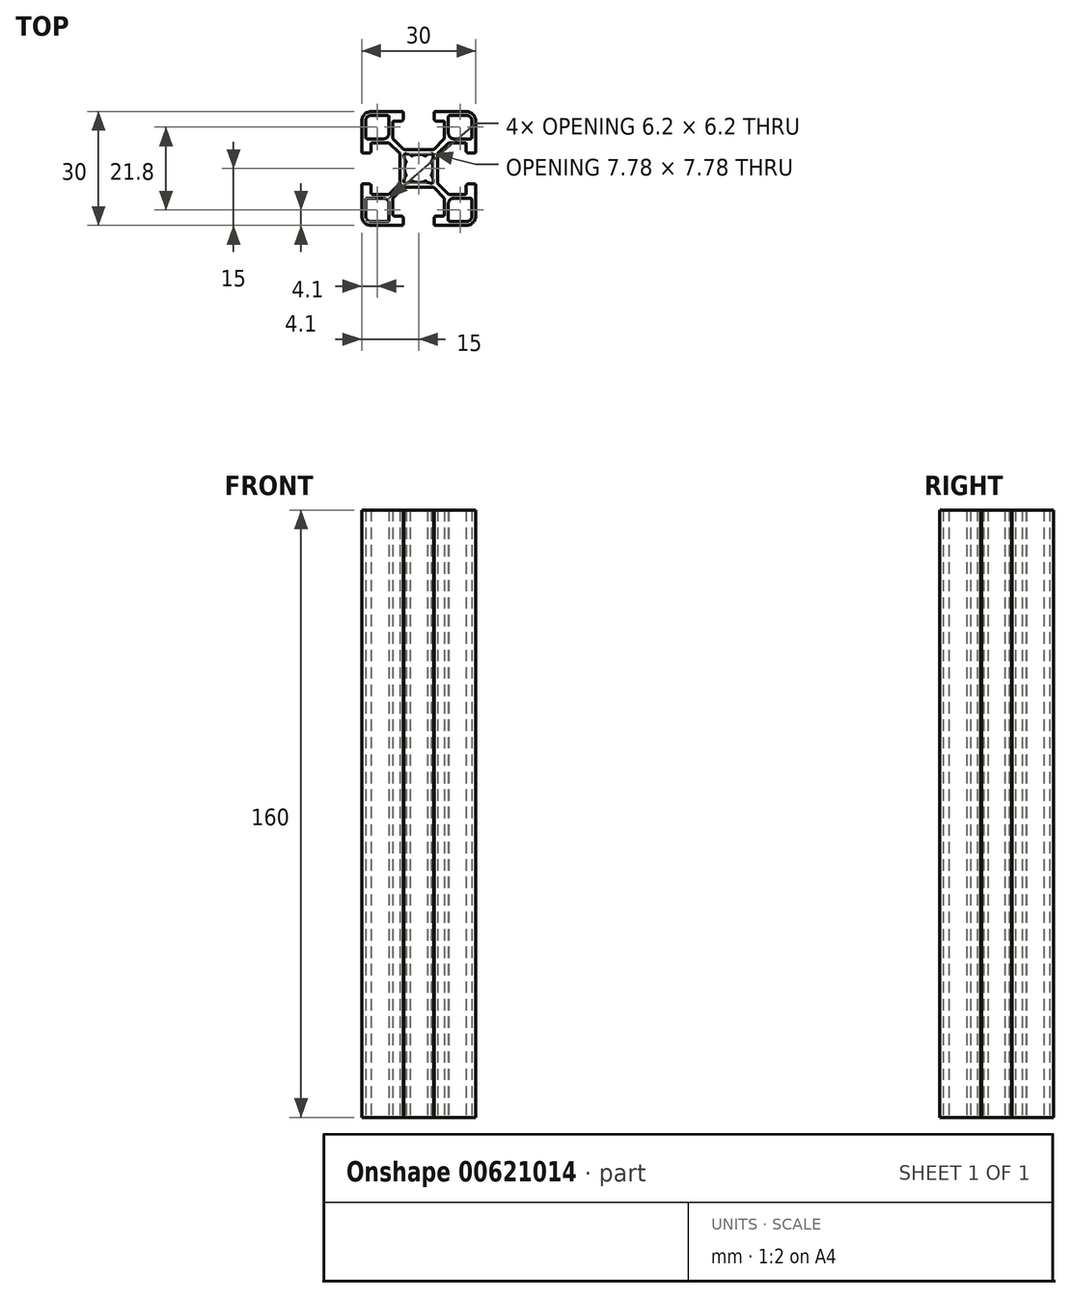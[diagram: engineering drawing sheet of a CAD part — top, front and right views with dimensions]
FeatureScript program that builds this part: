
annotation { "Feature Type Name" : "Feature", "Feature Type Description" : "" }
export const myFeature = defineFeature(function(context is Context, id is Id, definition is map)
    precondition{}
    {
        {
            var Q0;
            Q0=qCreatedBy(makeId("Top.planeOp"),FACE);
            var sketch = newSketch(context, id + "F0", { "sketchPlane" : qUnion([Q0])});
            skLineSegment(sketch, "E0", {"start": v(3.88, -3.29) * mm, "end": v(3.66, -2.24) * mm});
            skLineSegment(sketch, "E1", {"start": v(-3.66, 2.24) * mm, "end": v(-3.88, 3.29) * mm});
            skLineSegment(sketch, "E2", {"start": v(-2, 3.42) * mm, "end": v(-2.24, 3.66) * mm});
            skLineSegment(sketch, "E3", {"start": v(6.8, -7.86) * mm, "end": v(3.94, -5) * mm});
            skLineSegment(sketch, "E4", {"start": v(7.86, -6.8) * mm, "end": v(5, -3.94) * mm});
            skLineSegment(sketch, "E5", {"start": v(-3.42, 2) * mm, "end": v(-3.66, 2.24) * mm});
            skLineSegment(sketch, "E6", {"start": v(2.24, -3.66) * mm, "end": v(2, -3.42) * mm});
            skLineSegment(sketch, "E7", {"start": v(-5, 3.94) * mm, "end": v(-7.86, 6.8) * mm});
            skLineSegment(sketch, "E8", {"start": v(-3.94, 5) * mm, "end": v(-6.8, 7.86) * mm});
            skLineSegment(sketch, "E9", {"start": v(3.66, -2.24) * mm, "end": v(3.42, -2) * mm});
            skLineSegment(sketch, "E10", {"start": v(3.29, -3.88) * mm, "end": v(2.24, -3.66) * mm});
            skLineSegment(sketch, "E11", {"start": v(-2.24, 3.66) * mm, "end": v(-3.29, 3.88) * mm});
            skLineSegment(sketch, "E12", {"start": v(-12.5, -15) * mm, "end": v(-4.4, -15) * mm});
            skLineSegment(sketch, "E13", {"start": v(4.4, -15) * mm, "end": v(12.5, -15) * mm});
            skLineSegment(sketch, "E14", {"start": v(8.3, -14) * mm, "end": v(12.5, -14) * mm});
            skLineSegment(sketch, "E15", {"start": v(-12.5, -14) * mm, "end": v(-8.3, -14) * mm});
            skLineSegment(sketch, "E16", {"start": v(-6.5, -12.5) * mm, "end": v(-4.6, -12.5) * mm});
            skLineSegment(sketch, "E17", {"start": v(4.6, -12.5) * mm, "end": v(6.5, -12.5) * mm});
            skLineSegment(sketch, "E18", {"start": v(9.3, -7.8) * mm, "end": v(13.5, -7.8) * mm});
            skLineSegment(sketch, "E19", {"start": v(-13.5, -7.8) * mm, "end": v(-9.3, -7.8) * mm});
            skLineSegment(sketch, "E20", {"start": v(-12.2, -6.8) * mm, "end": v(-7.86, -6.8) * mm});
            skLineSegment(sketch, "E21", {"start": v(7.86, -6.8) * mm, "end": v(12.2, -6.8) * mm});
            skLineSegment(sketch, "E22", {"start": v(-3.94, -5) * mm, "end": v(3.94, -5) * mm});
            skLineSegment(sketch, "E23", {"start": v(-14.7, -4.1) * mm, "end": v(-13, -4.1) * mm});
            skLineSegment(sketch, "E24", {"start": v(13, -4.1) * mm, "end": v(14.7, -4.1) * mm});
            skLineSegment(sketch, "E25", {"start": v(-14.7, 4.1) * mm, "end": v(-13, 4.1) * mm});
            skLineSegment(sketch, "E26", {"start": v(13, 4.1) * mm, "end": v(14.7, 4.1) * mm});
            skLineSegment(sketch, "E27", {"start": v(-3.94, 5) * mm, "end": v(3.94, 5) * mm});
            skLineSegment(sketch, "E28", {"start": v(-12.2, 6.8) * mm, "end": v(-7.86, 6.8) * mm});
            skLineSegment(sketch, "E29", {"start": v(7.86, 6.8) * mm, "end": v(12.2, 6.8) * mm});
            skLineSegment(sketch, "E30", {"start": v(-13.5, 7.8) * mm, "end": v(-9.3, 7.8) * mm});
            skLineSegment(sketch, "E31", {"start": v(9.3, 7.8) * mm, "end": v(13.5, 7.8) * mm});
            skLineSegment(sketch, "E32", {"start": v(4.6, 12.5) * mm, "end": v(6.5, 12.5) * mm});
            skLineSegment(sketch, "E33", {"start": v(-6.5, 12.5) * mm, "end": v(-4.6, 12.5) * mm});
            skLineSegment(sketch, "E34", {"start": v(-12.5, 14) * mm, "end": v(-8.3, 14) * mm});
            skLineSegment(sketch, "E35", {"start": v(8.3, 14) * mm, "end": v(12.5, 14) * mm});
            skLineSegment(sketch, "E36", {"start": v(4.4, 15) * mm, "end": v(12.5, 15) * mm});
            skLineSegment(sketch, "E37", {"start": v(-12.5, 15) * mm, "end": v(-4.4, 15) * mm});
            skLineSegment(sketch, "E38", {"start": v(-3.29, -3.88) * mm, "end": v(-2.24, -3.66) * mm});
            skLineSegment(sketch, "E39", {"start": v(2.24, 3.66) * mm, "end": v(3.29, 3.88) * mm});
            skLineSegment(sketch, "E40", {"start": v(3.42, 2) * mm, "end": v(3.66, 2.24) * mm});
            skLineSegment(sketch, "E41", {"start": v(-6.8, -7.86) * mm, "end": v(-3.94, -5) * mm});
            skLineSegment(sketch, "E42", {"start": v(-7.86, -6.8) * mm, "end": v(-5, -3.94) * mm});
            skLineSegment(sketch, "E43", {"start": v(-2.24, -3.66) * mm, "end": v(-2, -3.42) * mm});
            skLineSegment(sketch, "E44", {"start": v(-3.66, -2.24) * mm, "end": v(-3.42, -2) * mm});
            skLineSegment(sketch, "E45", {"start": v(5, 3.94) * mm, "end": v(7.86, 6.8) * mm});
            skLineSegment(sketch, "E46", {"start": v(3.94, 5) * mm, "end": v(6.8, 7.86) * mm});
            skLineSegment(sketch, "E47", {"start": v(2, 3.42) * mm, "end": v(2.24, 3.66) * mm});
            skLineSegment(sketch, "E48", {"start": v(-3.88, -3.29) * mm, "end": v(-3.66, -2.24) * mm});
            skLineSegment(sketch, "E49", {"start": v(3.66, 2.24) * mm, "end": v(3.88, 3.29) * mm});
            skLineSegment(sketch, "E50", {"start": v(-15, 4.4) * mm, "end": v(-15, 12.5) * mm});
            skLineSegment(sketch, "E51", {"start": v(-15, -12.5) * mm, "end": v(-15, -4.4) * mm});
            skLineSegment(sketch, "E52", {"start": v(-14, 8.3) * mm, "end": v(-14, 12.5) * mm});
            skLineSegment(sketch, "E53", {"start": v(-14, -12.5) * mm, "end": v(-14, -8.3) * mm});
            skLineSegment(sketch, "E54", {"start": v(-12.5, -6.5) * mm, "end": v(-12.5, -4.6) * mm});
            skLineSegment(sketch, "E55", {"start": v(-12.5, 4.6) * mm, "end": v(-12.5, 6.5) * mm});
            skLineSegment(sketch, "E56", {"start": v(-7.8, 9.3) * mm, "end": v(-7.8, 13.5) * mm});
            skLineSegment(sketch, "E57", {"start": v(-7.8, -13.5) * mm, "end": v(-7.8, -9.3) * mm});
            skLineSegment(sketch, "E58", {"start": v(-6.8, -12.2) * mm, "end": v(-6.8, -7.86) * mm});
            skLineSegment(sketch, "E59", {"start": v(-6.8, 7.86) * mm, "end": v(-6.8, 12.2) * mm});
            skLineSegment(sketch, "E60", {"start": v(-5, -3.94) * mm, "end": v(-5, 3.94) * mm});
            skLineSegment(sketch, "E61", {"start": v(-4.1, -14.7) * mm, "end": v(-4.1, -13) * mm});
            skLineSegment(sketch, "E62", {"start": v(-4.1, 13) * mm, "end": v(-4.1, 14.7) * mm});
            skLineSegment(sketch, "E63", {"start": v(4.1, -14.7) * mm, "end": v(4.1, -13) * mm});
            skLineSegment(sketch, "E64", {"start": v(4.1, 13) * mm, "end": v(4.1, 14.7) * mm});
            skLineSegment(sketch, "E65", {"start": v(5, -3.94) * mm, "end": v(5, 3.94) * mm});
            skLineSegment(sketch, "E66", {"start": v(6.8, -12.2) * mm, "end": v(6.8, -7.86) * mm});
            skLineSegment(sketch, "E67", {"start": v(6.8, 7.86) * mm, "end": v(6.8, 12.2) * mm});
            skLineSegment(sketch, "E68", {"start": v(7.8, 9.3) * mm, "end": v(7.8, 13.5) * mm});
            skLineSegment(sketch, "E69", {"start": v(7.8, -13.5) * mm, "end": v(7.8, -9.3) * mm});
            skLineSegment(sketch, "E70", {"start": v(12.5, -6.5) * mm, "end": v(12.5, -4.6) * mm});
            skLineSegment(sketch, "E71", {"start": v(12.5, 4.6) * mm, "end": v(12.5, 6.5) * mm});
            skLineSegment(sketch, "E72", {"start": v(14, 8.3) * mm, "end": v(14, 12.5) * mm});
            skLineSegment(sketch, "E73", {"start": v(14, -12.5) * mm, "end": v(14, -8.3) * mm});
            skLineSegment(sketch, "E74", {"start": v(15, -12.5) * mm, "end": v(15, -4.4) * mm});
            skLineSegment(sketch, "E75", {"start": v(15, 4.4) * mm, "end": v(15, 12.5) * mm});
            skArc(sketch, "E76", {"start": v(-14.7, -4.1) * mm, "mid": v(-14.91, -4.19) * mm, "end": v(-15, -4.4) * mm});
            skArc(sketch, "E77", {"start": v(-15, 4.4) * mm, "mid": v(-14.91, 4.19) * mm, "end": v(-14.7, 4.1) * mm});
            skArc(sketch, "E78", {"start": v(-13.5, -7.8) * mm, "mid": v(-13.85, -7.95) * mm, "end": v(-14, -8.3) * mm});
            skArc(sketch, "E79", {"start": v(-14, 8.3) * mm, "mid": v(-13.85, 7.95) * mm, "end": v(-13.5, 7.8) * mm});
            skArc(sketch, "E80", {"start": v(-12.5, -4.6) * mm, "mid": v(-12.65, -4.25) * mm, "end": v(-13, -4.1) * mm});
            skArc(sketch, "E81", {"start": v(-13, 4.1) * mm, "mid": v(-12.65, 4.25) * mm, "end": v(-12.5, 4.6) * mm});
            skArc(sketch, "E82", {"start": v(-14, -12.5) * mm, "mid": v(-13.56, -13.56) * mm, "end": v(-12.5, -14) * mm});
            skArc(sketch, "E83", {"start": v(-15, -12.5) * mm, "mid": v(-14.27, -14.27) * mm, "end": v(-12.5, -15) * mm});
            skArc(sketch, "E84", {"start": v(-12.5, 14) * mm, "mid": v(-13.56, 13.56) * mm, "end": v(-14, 12.5) * mm});
            skArc(sketch, "E85", {"start": v(-12.5, 15) * mm, "mid": v(-14.27, 14.27) * mm, "end": v(-15, 12.5) * mm});
            skArc(sketch, "E86", {"start": v(-12.5, -6.5) * mm, "mid": v(-12.41, -6.71) * mm, "end": v(-12.2, -6.8) * mm});
            skArc(sketch, "E87", {"start": v(-12.2, 6.8) * mm, "mid": v(-12.41, 6.71) * mm, "end": v(-12.5, 6.5) * mm});
            skArc(sketch, "E88", {"start": v(-7.8, -9.3) * mm, "mid": v(-8.24, -8.24) * mm, "end": v(-9.3, -7.8) * mm});
            skArc(sketch, "E89", {"start": v(-9.3, 7.8) * mm, "mid": v(-8.24, 8.24) * mm, "end": v(-7.8, 9.3) * mm});
            skArc(sketch, "E90", {"start": v(-8.3, -14) * mm, "mid": v(-7.95, -13.85) * mm, "end": v(-7.8, -13.5) * mm});
            skArc(sketch, "E91", {"start": v(-7.8, 13.5) * mm, "mid": v(-7.95, 13.85) * mm, "end": v(-8.3, 14) * mm});
            skArc(sketch, "E92", {"start": v(-6.8, -12.2) * mm, "mid": v(-6.71, -12.41) * mm, "end": v(-6.5, -12.5) * mm});
            skArc(sketch, "E93", {"start": v(-6.5, 12.5) * mm, "mid": v(-6.71, 12.41) * mm, "end": v(-6.8, 12.2) * mm});
            skArc(sketch, "E94", {"start": v(-4.1, -13) * mm, "mid": v(-4.25, -12.65) * mm, "end": v(-4.6, -12.5) * mm});
            skArc(sketch, "E95", {"start": v(-4.6, 12.5) * mm, "mid": v(-4.25, 12.65) * mm, "end": v(-4.1, 13) * mm});
            skArc(sketch, "E96", {"start": v(-4.4, -15) * mm, "mid": v(-4.19, -14.91) * mm, "end": v(-4.1, -14.7) * mm});
            skArc(sketch, "E97", {"start": v(-4.1, 14.7) * mm, "mid": v(-4.19, 14.91) * mm, "end": v(-4.4, 15) * mm});
            skArc(sketch, "E98", {"start": v(-3.42, -2) * mm, "mid": v(-3.34, -1.84) * mm, "end": v(-3.36, -1.66) * mm});
            skArc(sketch, "E99", {"start": v(-3.36, 1.66) * mm, "mid": v(-3.34, 1.84) * mm, "end": v(-3.42, 2) * mm});
            skArc(sketch, "E100", {"start": v(-3.88, -3.29) * mm, "mid": v(-3.74, -3.74) * mm, "end": v(-3.29, -3.88) * mm});
            skArc(sketch, "E101", {"start": v(-3.29, 3.88) * mm, "mid": v(-3.74, 3.74) * mm, "end": v(-3.88, 3.29) * mm});
            skArc(sketch, "E102", {"start": v(-1.66, -3.36) * mm, "mid": v(-1.84, -3.34) * mm, "end": v(-2, -3.42) * mm});
            skArc(sketch, "E103", {"start": v(-2, 3.42) * mm, "mid": v(-1.84, 3.34) * mm, "end": v(-1.66, 3.36) * mm});
            skArc(sketch, "E104", {"start": v(-3.36, 1.66) * mm, "mid": v(-3.75, 0) * mm, "end": v(-3.36, -1.66) * mm});
            skArc(sketch, "E105", {"start": v(1.66, 3.36) * mm, "mid": v(0, 3.75) * mm, "end": v(-1.66, 3.36) * mm});
            skArc(sketch, "E106", {"start": v(3.36, -1.66) * mm, "mid": v(3.75, 0) * mm, "end": v(3.36, 1.66) * mm});
            skArc(sketch, "E107", {"start": v(-1.66, -3.36) * mm, "mid": v(0, -3.75) * mm, "end": v(1.66, -3.36) * mm});
            skArc(sketch, "E108", {"start": v(2, -3.42) * mm, "mid": v(1.84, -3.34) * mm, "end": v(1.66, -3.36) * mm});
            skArc(sketch, "E109", {"start": v(1.66, 3.36) * mm, "mid": v(1.84, 3.34) * mm, "end": v(2, 3.42) * mm});
            skArc(sketch, "E110", {"start": v(3.29, -3.88) * mm, "mid": v(3.74, -3.74) * mm, "end": v(3.88, -3.29) * mm});
            skArc(sketch, "E111", {"start": v(3.88, 3.29) * mm, "mid": v(3.74, 3.74) * mm, "end": v(3.29, 3.88) * mm});
            skArc(sketch, "E112", {"start": v(3.36, -1.66) * mm, "mid": v(3.34, -1.84) * mm, "end": v(3.42, -2) * mm});
            skArc(sketch, "E113", {"start": v(3.42, 2) * mm, "mid": v(3.34, 1.84) * mm, "end": v(3.36, 1.66) * mm});
            skArc(sketch, "E114", {"start": v(4.1, -14.7) * mm, "mid": v(4.19, -14.91) * mm, "end": v(4.4, -15) * mm});
            skArc(sketch, "E115", {"start": v(4.4, 15) * mm, "mid": v(4.19, 14.91) * mm, "end": v(4.1, 14.7) * mm});
            skArc(sketch, "E116", {"start": v(4.6, -12.5) * mm, "mid": v(4.25, -12.65) * mm, "end": v(4.1, -13) * mm});
            skArc(sketch, "E117", {"start": v(4.1, 13) * mm, "mid": v(4.25, 12.65) * mm, "end": v(4.6, 12.5) * mm});
            skArc(sketch, "E118", {"start": v(6.5, -12.5) * mm, "mid": v(6.71, -12.41) * mm, "end": v(6.8, -12.2) * mm});
            skArc(sketch, "E119", {"start": v(6.8, 12.2) * mm, "mid": v(6.71, 12.41) * mm, "end": v(6.5, 12.5) * mm});
            skArc(sketch, "E120", {"start": v(7.8, -13.5) * mm, "mid": v(7.95, -13.85) * mm, "end": v(8.3, -14) * mm});
            skArc(sketch, "E121", {"start": v(8.3, 14) * mm, "mid": v(7.95, 13.85) * mm, "end": v(7.8, 13.5) * mm});
            skArc(sketch, "E122", {"start": v(9.3, -7.8) * mm, "mid": v(8.24, -8.24) * mm, "end": v(7.8, -9.3) * mm});
            skArc(sketch, "E123", {"start": v(7.8, 9.3) * mm, "mid": v(8.24, 8.24) * mm, "end": v(9.3, 7.8) * mm});
            skArc(sketch, "E124", {"start": v(12.2, -6.8) * mm, "mid": v(12.41, -6.71) * mm, "end": v(12.5, -6.5) * mm});
            skArc(sketch, "E125", {"start": v(12.5, 6.5) * mm, "mid": v(12.41, 6.71) * mm, "end": v(12.2, 6.8) * mm});
            skArc(sketch, "E126", {"start": v(12.5, -14) * mm, "mid": v(13.56, -13.56) * mm, "end": v(14, -12.5) * mm});
            skArc(sketch, "E127", {"start": v(12.5, -15) * mm, "mid": v(14.27, -14.27) * mm, "end": v(15, -12.5) * mm});
            skArc(sketch, "E128", {"start": v(14, 12.5) * mm, "mid": v(13.56, 13.56) * mm, "end": v(12.5, 14) * mm});
            skArc(sketch, "E129", {"start": v(15, 12.5) * mm, "mid": v(14.27, 14.27) * mm, "end": v(12.5, 15) * mm});
            skArc(sketch, "E130", {"start": v(13, -4.1) * mm, "mid": v(12.65, -4.25) * mm, "end": v(12.5, -4.6) * mm});
            skArc(sketch, "E131", {"start": v(12.5, 4.6) * mm, "mid": v(12.65, 4.25) * mm, "end": v(13, 4.1) * mm});
            skArc(sketch, "E132", {"start": v(14, -8.3) * mm, "mid": v(13.85, -7.95) * mm, "end": v(13.5, -7.8) * mm});
            skArc(sketch, "E133", {"start": v(13.5, 7.8) * mm, "mid": v(13.85, 7.95) * mm, "end": v(14, 8.3) * mm});
            skArc(sketch, "E134", {"start": v(15, -4.4) * mm, "mid": v(14.91, -4.19) * mm, "end": v(14.7, -4.1) * mm});
            skArc(sketch, "E135", {"start": v(14.7, 4.1) * mm, "mid": v(14.91, 4.19) * mm, "end": v(15, 4.4) * mm});
            skSolve(sketch);
        }
        {
            var Q0;
            Q0=makeQuery(id+"F0.imprint","IMPRINT",FACE,{"disambiguationData":[TD([[makeQuery(id+"F0.imprint","IMPRINT",EDGE,{"derivedFrom":sQuery(id+"F0.wireOp",EDGE,"E0")}),-1.0]])]});
            extrude(context, id + "F1", {"entities" : qUnion([Q0]), "depth" : 160 * mm, "offsetDistance" : 25 * mm});
        }
        {
            var Q0;
            Q0=makeQuery(id+"F1.opExtrude","CAP_FACE",FACE,{"disambiguationData":[OSD([sQuery(id+"F0.wireOp",EDGE,"E0"),sQuery(id+"F0.wireOp",EDGE,"E1"),sQuery(id+"F0.wireOp",EDGE,"E2"),sQuery(id+"F0.wireOp",EDGE,"E3"),sQuery(id+"F0.wireOp",EDGE,"E4"),sQuery(id+"F0.wireOp",EDGE,"E5"),sQuery(id+"F0.wireOp",EDGE,"E6"),sQuery(id+"F0.wireOp",EDGE,"E7"),sQuery(id+"F0.wireOp",EDGE,"E8"),sQuery(id+"F0.wireOp",EDGE,"E9"),sQuery(id+"F0.wireOp",EDGE,"E10"),sQuery(id+"F0.wireOp",EDGE,"E11"),sQuery(id+"F0.wireOp",EDGE,"E12"),sQuery(id+"F0.wireOp",EDGE,"E13"),sQuery(id+"F0.wireOp",EDGE,"E14"),sQuery(id+"F0.wireOp",EDGE,"E15"),sQuery(id+"F0.wireOp",EDGE,"E16"),sQuery(id+"F0.wireOp",EDGE,"E17"),sQuery(id+"F0.wireOp",EDGE,"E18"),sQuery(id+"F0.wireOp",EDGE,"E19"),sQuery(id+"F0.wireOp",EDGE,"E20"),sQuery(id+"F0.wireOp",EDGE,"E21"),sQuery(id+"F0.wireOp",EDGE,"E22"),sQuery(id+"F0.wireOp",EDGE,"E23"),sQuery(id+"F0.wireOp",EDGE,"E24"),sQuery(id+"F0.wireOp",EDGE,"E25"),sQuery(id+"F0.wireOp",EDGE,"E26"),sQuery(id+"F0.wireOp",EDGE,"E27"),sQuery(id+"F0.wireOp",EDGE,"E28"),sQuery(id+"F0.wireOp",EDGE,"E29"),sQuery(id+"F0.wireOp",EDGE,"E30"),sQuery(id+"F0.wireOp",EDGE,"E31"),sQuery(id+"F0.wireOp",EDGE,"E32"),sQuery(id+"F0.wireOp",EDGE,"E33"),sQuery(id+"F0.wireOp",EDGE,"E34"),sQuery(id+"F0.wireOp",EDGE,"E35"),sQuery(id+"F0.wireOp",EDGE,"E36"),sQuery(id+"F0.wireOp",EDGE,"E37"),sQuery(id+"F0.wireOp",EDGE,"E38"),sQuery(id+"F0.wireOp",EDGE,"E39"),sQuery(id+"F0.wireOp",EDGE,"E40"),sQuery(id+"F0.wireOp",EDGE,"E41"),sQuery(id+"F0.wireOp",EDGE,"E42"),sQuery(id+"F0.wireOp",EDGE,"E43"),sQuery(id+"F0.wireOp",EDGE,"E44"),sQuery(id+"F0.wireOp",EDGE,"E45"),sQuery(id+"F0.wireOp",EDGE,"E46"),sQuery(id+"F0.wireOp",EDGE,"E47"),sQuery(id+"F0.wireOp",EDGE,"E48"),sQuery(id+"F0.wireOp",EDGE,"E49"),sQuery(id+"F0.wireOp",EDGE,"E50"),sQuery(id+"F0.wireOp",EDGE,"E51"),sQuery(id+"F0.wireOp",EDGE,"E52"),sQuery(id+"F0.wireOp",EDGE,"E53"),sQuery(id+"F0.wireOp",EDGE,"E54"),sQuery(id+"F0.wireOp",EDGE,"E55"),sQuery(id+"F0.wireOp",EDGE,"E56"),sQuery(id+"F0.wireOp",EDGE,"E57"),sQuery(id+"F0.wireOp",EDGE,"E58"),sQuery(id+"F0.wireOp",EDGE,"E59"),sQuery(id+"F0.wireOp",EDGE,"E60"),sQuery(id+"F0.wireOp",EDGE,"E61"),sQuery(id+"F0.wireOp",EDGE,"E62"),sQuery(id+"F0.wireOp",EDGE,"E63"),sQuery(id+"F0.wireOp",EDGE,"E64"),sQuery(id+"F0.wireOp",EDGE,"E65"),sQuery(id+"F0.wireOp",EDGE,"E66"),sQuery(id+"F0.wireOp",EDGE,"E67"),sQuery(id+"F0.wireOp",EDGE,"E68"),sQuery(id+"F0.wireOp",EDGE,"E69"),sQuery(id+"F0.wireOp",EDGE,"E70"),sQuery(id+"F0.wireOp",EDGE,"E71"),sQuery(id+"F0.wireOp",EDGE,"E72"),sQuery(id+"F0.wireOp",EDGE,"E73"),sQuery(id+"F0.wireOp",EDGE,"E74"),sQuery(id+"F0.wireOp",EDGE,"E75"),sQuery(id+"F0.wireOp",EDGE,"E76"),sQuery(id+"F0.wireOp",EDGE,"E77"),sQuery(id+"F0.wireOp",EDGE,"E78"),sQuery(id+"F0.wireOp",EDGE,"E79"),sQuery(id+"F0.wireOp",EDGE,"E80"),sQuery(id+"F0.wireOp",EDGE,"E81"),sQuery(id+"F0.wireOp",EDGE,"E82"),sQuery(id+"F0.wireOp",EDGE,"E83"),sQuery(id+"F0.wireOp",EDGE,"E84"),sQuery(id+"F0.wireOp",EDGE,"E85"),sQuery(id+"F0.wireOp",EDGE,"E86"),sQuery(id+"F0.wireOp",EDGE,"E87"),sQuery(id+"F0.wireOp",EDGE,"E88"),sQuery(id+"F0.wireOp",EDGE,"E89"),sQuery(id+"F0.wireOp",EDGE,"E90"),sQuery(id+"F0.wireOp",EDGE,"E91"),sQuery(id+"F0.wireOp",EDGE,"E92"),sQuery(id+"F0.wireOp",EDGE,"E93"),sQuery(id+"F0.wireOp",EDGE,"E94"),sQuery(id+"F0.wireOp",EDGE,"E95"),sQuery(id+"F0.wireOp",EDGE,"E96"),sQuery(id+"F0.wireOp",EDGE,"E97"),sQuery(id+"F0.wireOp",EDGE,"E98"),sQuery(id+"F0.wireOp",EDGE,"E99"),sQuery(id+"F0.wireOp",EDGE,"E100"),sQuery(id+"F0.wireOp",EDGE,"E101"),sQuery(id+"F0.wireOp",EDGE,"E102"),sQuery(id+"F0.wireOp",EDGE,"E103"),sQuery(id+"F0.wireOp",EDGE,"E104"),sQuery(id+"F0.wireOp",EDGE,"E105"),sQuery(id+"F0.wireOp",EDGE,"E106"),sQuery(id+"F0.wireOp",EDGE,"E107"),sQuery(id+"F0.wireOp",EDGE,"E108"),sQuery(id+"F0.wireOp",EDGE,"E109"),sQuery(id+"F0.wireOp",EDGE,"E110"),sQuery(id+"F0.wireOp",EDGE,"E111"),sQuery(id+"F0.wireOp",EDGE,"E112"),sQuery(id+"F0.wireOp",EDGE,"E113"),sQuery(id+"F0.wireOp",EDGE,"E114"),sQuery(id+"F0.wireOp",EDGE,"E115"),sQuery(id+"F0.wireOp",EDGE,"E116"),sQuery(id+"F0.wireOp",EDGE,"E117"),sQuery(id+"F0.wireOp",EDGE,"E118"),sQuery(id+"F0.wireOp",EDGE,"E119"),sQuery(id+"F0.wireOp",EDGE,"E120"),sQuery(id+"F0.wireOp",EDGE,"E121"),sQuery(id+"F0.wireOp",EDGE,"E122"),sQuery(id+"F0.wireOp",EDGE,"E123"),sQuery(id+"F0.wireOp",EDGE,"E124"),sQuery(id+"F0.wireOp",EDGE,"E125"),sQuery(id+"F0.wireOp",EDGE,"E126"),sQuery(id+"F0.wireOp",EDGE,"E127"),sQuery(id+"F0.wireOp",EDGE,"E128"),sQuery(id+"F0.wireOp",EDGE,"E129"),sQuery(id+"F0.wireOp",EDGE,"E130"),sQuery(id+"F0.wireOp",EDGE,"E131"),sQuery(id+"F0.wireOp",EDGE,"E132"),sQuery(id+"F0.wireOp",EDGE,"E133"),sQuery(id+"F0.wireOp",EDGE,"E134"),sQuery(id+"F0.wireOp",EDGE,"E135")])],"isStart":true});
            var sketch = newSketch(context, id + "F2", { "sketchPlane" : qUnion([Q0])});
            skLineSegment(sketch, "E136", {"start": v(15, -4.4) * mm, "end": v(15, 4.4) * mm});
            skSolve(sketch);
        }
        {
            var Q0;
            Q0=sQuery(id+"F2.wireOp",EDGE,"E136");
            var Q1;
            Q1=makeQuery(id+"F1.opExtrude","CAP_FACE",FACE,{"disambiguationData":[OSD([sQuery(id+"F0.wireOp",EDGE,"E0"),sQuery(id+"F0.wireOp",EDGE,"E1"),sQuery(id+"F0.wireOp",EDGE,"E2"),sQuery(id+"F0.wireOp",EDGE,"E3"),sQuery(id+"F0.wireOp",EDGE,"E4"),sQuery(id+"F0.wireOp",EDGE,"E5"),sQuery(id+"F0.wireOp",EDGE,"E6"),sQuery(id+"F0.wireOp",EDGE,"E7"),sQuery(id+"F0.wireOp",EDGE,"E8"),sQuery(id+"F0.wireOp",EDGE,"E9"),sQuery(id+"F0.wireOp",EDGE,"E10"),sQuery(id+"F0.wireOp",EDGE,"E11"),sQuery(id+"F0.wireOp",EDGE,"E12"),sQuery(id+"F0.wireOp",EDGE,"E13"),sQuery(id+"F0.wireOp",EDGE,"E14"),sQuery(id+"F0.wireOp",EDGE,"E15"),sQuery(id+"F0.wireOp",EDGE,"E16"),sQuery(id+"F0.wireOp",EDGE,"E17"),sQuery(id+"F0.wireOp",EDGE,"E18"),sQuery(id+"F0.wireOp",EDGE,"E19"),sQuery(id+"F0.wireOp",EDGE,"E20"),sQuery(id+"F0.wireOp",EDGE,"E21"),sQuery(id+"F0.wireOp",EDGE,"E22"),sQuery(id+"F0.wireOp",EDGE,"E23"),sQuery(id+"F0.wireOp",EDGE,"E24"),sQuery(id+"F0.wireOp",EDGE,"E25"),sQuery(id+"F0.wireOp",EDGE,"E26"),sQuery(id+"F0.wireOp",EDGE,"E27"),sQuery(id+"F0.wireOp",EDGE,"E28"),sQuery(id+"F0.wireOp",EDGE,"E29"),sQuery(id+"F0.wireOp",EDGE,"E30"),sQuery(id+"F0.wireOp",EDGE,"E31"),sQuery(id+"F0.wireOp",EDGE,"E32"),sQuery(id+"F0.wireOp",EDGE,"E33"),sQuery(id+"F0.wireOp",EDGE,"E34"),sQuery(id+"F0.wireOp",EDGE,"E35"),sQuery(id+"F0.wireOp",EDGE,"E36"),sQuery(id+"F0.wireOp",EDGE,"E37"),sQuery(id+"F0.wireOp",EDGE,"E38"),sQuery(id+"F0.wireOp",EDGE,"E39"),sQuery(id+"F0.wireOp",EDGE,"E40"),sQuery(id+"F0.wireOp",EDGE,"E41"),sQuery(id+"F0.wireOp",EDGE,"E42"),sQuery(id+"F0.wireOp",EDGE,"E43"),sQuery(id+"F0.wireOp",EDGE,"E44"),sQuery(id+"F0.wireOp",EDGE,"E45"),sQuery(id+"F0.wireOp",EDGE,"E46"),sQuery(id+"F0.wireOp",EDGE,"E47"),sQuery(id+"F0.wireOp",EDGE,"E48"),sQuery(id+"F0.wireOp",EDGE,"E49"),sQuery(id+"F0.wireOp",EDGE,"E50"),sQuery(id+"F0.wireOp",EDGE,"E51"),sQuery(id+"F0.wireOp",EDGE,"E52"),sQuery(id+"F0.wireOp",EDGE,"E53"),sQuery(id+"F0.wireOp",EDGE,"E54"),sQuery(id+"F0.wireOp",EDGE,"E55"),sQuery(id+"F0.wireOp",EDGE,"E56"),sQuery(id+"F0.wireOp",EDGE,"E57"),sQuery(id+"F0.wireOp",EDGE,"E58"),sQuery(id+"F0.wireOp",EDGE,"E59"),sQuery(id+"F0.wireOp",EDGE,"E60"),sQuery(id+"F0.wireOp",EDGE,"E61"),sQuery(id+"F0.wireOp",EDGE,"E62"),sQuery(id+"F0.wireOp",EDGE,"E63"),sQuery(id+"F0.wireOp",EDGE,"E64"),sQuery(id+"F0.wireOp",EDGE,"E65"),sQuery(id+"F0.wireOp",EDGE,"E66"),sQuery(id+"F0.wireOp",EDGE,"E67"),sQuery(id+"F0.wireOp",EDGE,"E68"),sQuery(id+"F0.wireOp",EDGE,"E69"),sQuery(id+"F0.wireOp",EDGE,"E70"),sQuery(id+"F0.wireOp",EDGE,"E71"),sQuery(id+"F0.wireOp",EDGE,"E72"),sQuery(id+"F0.wireOp",EDGE,"E73"),sQuery(id+"F0.wireOp",EDGE,"E74"),sQuery(id+"F0.wireOp",EDGE,"E75"),sQuery(id+"F0.wireOp",EDGE,"E76"),sQuery(id+"F0.wireOp",EDGE,"E77"),sQuery(id+"F0.wireOp",EDGE,"E78"),sQuery(id+"F0.wireOp",EDGE,"E79"),sQuery(id+"F0.wireOp",EDGE,"E80"),sQuery(id+"F0.wireOp",EDGE,"E81"),sQuery(id+"F0.wireOp",EDGE,"E82"),sQuery(id+"F0.wireOp",EDGE,"E83"),sQuery(id+"F0.wireOp",EDGE,"E84"),sQuery(id+"F0.wireOp",EDGE,"E85"),sQuery(id+"F0.wireOp",EDGE,"E86"),sQuery(id+"F0.wireOp",EDGE,"E87"),sQuery(id+"F0.wireOp",EDGE,"E88"),sQuery(id+"F0.wireOp",EDGE,"E89"),sQuery(id+"F0.wireOp",EDGE,"E90"),sQuery(id+"F0.wireOp",EDGE,"E91"),sQuery(id+"F0.wireOp",EDGE,"E92"),sQuery(id+"F0.wireOp",EDGE,"E93"),sQuery(id+"F0.wireOp",EDGE,"E94"),sQuery(id+"F0.wireOp",EDGE,"E95"),sQuery(id+"F0.wireOp",EDGE,"E96"),sQuery(id+"F0.wireOp",EDGE,"E97"),sQuery(id+"F0.wireOp",EDGE,"E98"),sQuery(id+"F0.wireOp",EDGE,"E99"),sQuery(id+"F0.wireOp",EDGE,"E100"),sQuery(id+"F0.wireOp",EDGE,"E101"),sQuery(id+"F0.wireOp",EDGE,"E102"),sQuery(id+"F0.wireOp",EDGE,"E103"),sQuery(id+"F0.wireOp",EDGE,"E104"),sQuery(id+"F0.wireOp",EDGE,"E105"),sQuery(id+"F0.wireOp",EDGE,"E106"),sQuery(id+"F0.wireOp",EDGE,"E107"),sQuery(id+"F0.wireOp",EDGE,"E108"),sQuery(id+"F0.wireOp",EDGE,"E109"),sQuery(id+"F0.wireOp",EDGE,"E110"),sQuery(id+"F0.wireOp",EDGE,"E111"),sQuery(id+"F0.wireOp",EDGE,"E112"),sQuery(id+"F0.wireOp",EDGE,"E113"),sQuery(id+"F0.wireOp",EDGE,"E114"),sQuery(id+"F0.wireOp",EDGE,"E115"),sQuery(id+"F0.wireOp",EDGE,"E116"),sQuery(id+"F0.wireOp",EDGE,"E117"),sQuery(id+"F0.wireOp",EDGE,"E118"),sQuery(id+"F0.wireOp",EDGE,"E119"),sQuery(id+"F0.wireOp",EDGE,"E120"),sQuery(id+"F0.wireOp",EDGE,"E121"),sQuery(id+"F0.wireOp",EDGE,"E122"),sQuery(id+"F0.wireOp",EDGE,"E123"),sQuery(id+"F0.wireOp",EDGE,"E124"),sQuery(id+"F0.wireOp",EDGE,"E125"),sQuery(id+"F0.wireOp",EDGE,"E126"),sQuery(id+"F0.wireOp",EDGE,"E127"),sQuery(id+"F0.wireOp",EDGE,"E128"),sQuery(id+"F0.wireOp",EDGE,"E129"),sQuery(id+"F0.wireOp",EDGE,"E130"),sQuery(id+"F0.wireOp",EDGE,"E131"),sQuery(id+"F0.wireOp",EDGE,"E132"),sQuery(id+"F0.wireOp",EDGE,"E133"),sQuery(id+"F0.wireOp",EDGE,"E134"),sQuery(id+"F0.wireOp",EDGE,"E135")])],"isStart":false});
            extrude(context, id + "F3", {"bodyType" : ToolBodyType.SURFACE, "surfaceEntities" : qUnion([Q0]), "endBound" : BoundingType.UP_TO_SURFACE, "oppositeDirection" : true, "depth" : 25 * mm, "endBoundEntityFace" : qUnion([Q1]), "offsetDistance" : 25 * mm});
        }
    });
